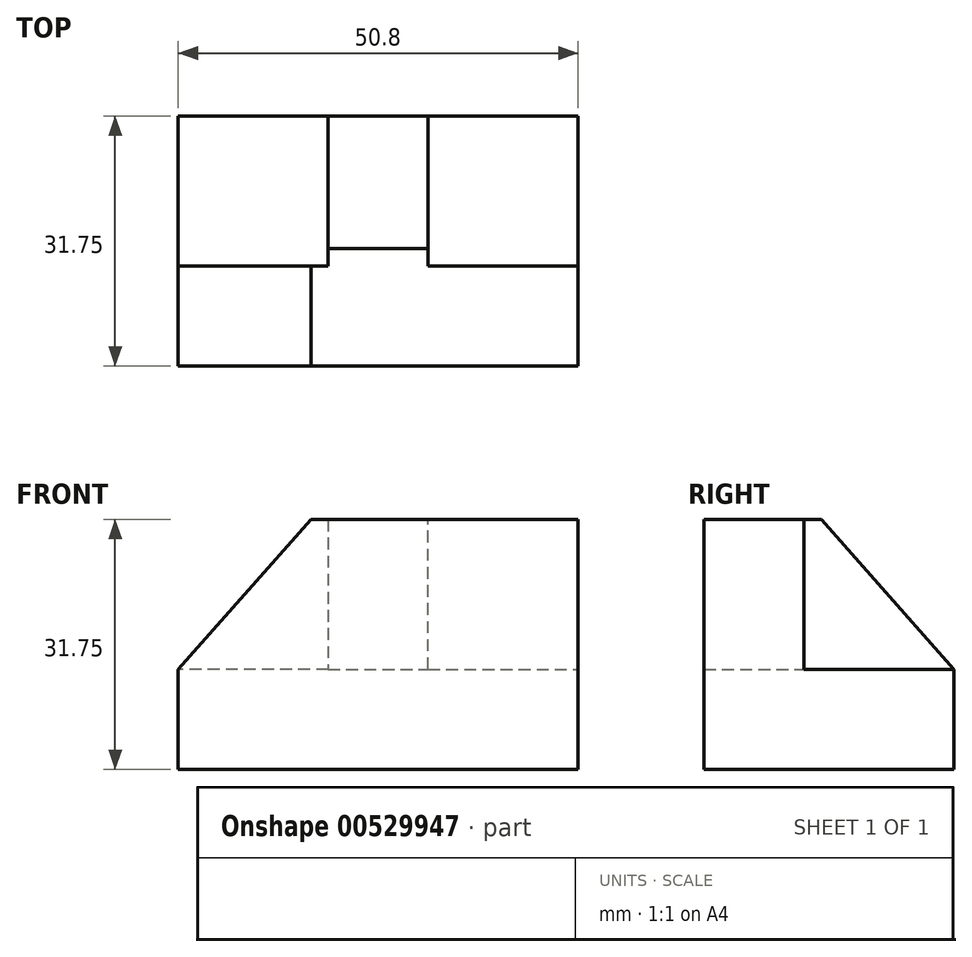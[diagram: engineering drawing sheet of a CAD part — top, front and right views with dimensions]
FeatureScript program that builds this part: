
annotation { "Feature Type Name" : "Feature", "Feature Type Description" : "" }
export const myFeature = defineFeature(function(context is Context, id is Id, definition is map)
    precondition{}
    {
        {
            var Q0;
            Q0=qCreatedBy(makeId("Front.planeOp"),FACE);
            var sketch = newSketch(context, id + "F0", { "sketchPlane" : qUnion([Q0])});
            skLineSegment(sketch, "E0", {"start": v(-58.65, 28.73) * mm, "end": v(-7.85, 28.73) * mm});
            skLineSegment(sketch, "E1", {"start": v(-7.85, 28.73) * mm, "end": v(-7.85, 60.48) * mm});
            skLineSegment(sketch, "E2", {"start": v(-7.85, 60.48) * mm, "end": v(-58.65, 60.48) * mm});
            skLineSegment(sketch, "E3", {"start": v(-58.65, 60.48) * mm, "end": v(-58.65, 28.73) * mm});
            skSolve(sketch);
        }
        {
            var Q0;
            Q0 = qSketchRegion(id + "F0", true);
            extrude(context, id + "F1", {"entities" : qUnion([Q0]), "depth" : 31.75 * mm, "offsetDistance" : 25.4 * mm});
        }
        {
            var Q0;
            Q0=makeQuery(id+"F1.opExtrude","SWEPT_FACE",FACE,{"disambiguationData":[OSD([sQuery(id+"F0.wireOp",EDGE,"E3")])]});
            var sketch = newSketch(context, id + "F2", { "sketchPlane" : qUnion([Q0])});
            skLineSegment(sketch, "E4", {"start": v(0, 28.73) * mm, "end": v(0, 41.46) * mm});
            skLineSegment(sketch, "E5", {"start": v(0, 41.46) * mm, "end": v(19.06, 41.46) * mm});
            skLineSegment(sketch, "E6", {"start": v(19.06, 41.46) * mm, "end": v(19.06, 60.48) * mm});
            skLineSegment(sketch, "E7", {"start": v(19.06, 60.48) * mm, "end": v(0, 60.48) * mm});
            skLineSegment(sketch, "E8", {"start": v(0, 60.48) * mm, "end": v(0, 41.46) * mm});
            skSolve(sketch);
        }
        {
            var Q0;
            Q0=makeQuery(id+"F2.imprint","IMPRINT",FACE,{"disambiguationData":[TD([[makeQuery(id+"F2.imprint","IMPRINT",EDGE,{"derivedFrom":sQuery(id+"F2.wireOp",EDGE,"E5")}),1.0]])]});
            extrude(context, id + "F3", {"entities" : qUnion([Q0]), "operationType" : NewBodyOperationType.REMOVE, "oppositeDirection" : true, "depth" : 19.05 * mm, "offsetDistance" : 25.4 * mm});
        }
        {
            var Q0;
            Q0=makeQuery(id+"F1.opExtrude","SWEPT_FACE",FACE,{"disambiguationData":[OSD([sQuery(id+"F0.wireOp",EDGE,"E1")])]});
            var sketch = newSketch(context, id + "F4", { "sketchPlane" : qUnion([Q0])});
            skLineSegment(sketch, "E9", {"start": v(0, 28.73) * mm, "end": v(0, 41.46) * mm});
            skLineSegment(sketch, "E10", {"start": v(0, 41.46) * mm, "end": v(-19.06, 41.46) * mm});
            skLineSegment(sketch, "E11", {"start": v(-19.06, 41.46) * mm, "end": v(-19.06, 60.48) * mm});
            skLineSegment(sketch, "E12", {"start": v(-19.06, 60.48) * mm, "end": v(0, 60.48) * mm});
            skLineSegment(sketch, "E13", {"start": v(0, 60.48) * mm, "end": v(0, 41.46) * mm});
            skSolve(sketch);
        }
        {
            var Q0;
            Q0=makeQuery(id+"F4.imprint","IMPRINT",FACE,{"disambiguationData":[TD([[makeQuery(id+"F4.imprint","IMPRINT",EDGE,{"derivedFrom":sQuery(id+"F4.wireOp",EDGE,"E10")}),-1.0]])]});
            extrude(context, id + "F5", {"entities" : qUnion([Q0]), "operationType" : NewBodyOperationType.REMOVE, "oppositeDirection" : true, "depth" : 19.05 * mm, "offsetDistance" : 25.4 * mm});
        }
        {
            var Q0;
            Q0=makeQuery(id+"F3.boolean.opBoolean","COPY",FACE,{"derivedFrom":makeQuery(id+"F3.opExtrude","SWEPT_FACE",FACE,{"disambiguationData":[OSD([sQuery(id+"F2.wireOp",EDGE,"E6")])]})});
            var sketch = newSketch(context, id + "F6", { "sketchPlane" : qUnion([Q0])});
            skLineSegment(sketch, "E14", {"start": v(58.65, 41.46) * mm, "end": v(41.8, 60.48) * mm});
            skLineSegment(sketch, "E15", {"start": v(41.8, 60.48) * mm, "end": v(58.65, 60.48) * mm});
            skLineSegment(sketch, "E16", {"start": v(58.65, 60.48) * mm, "end": v(58.65, 41.46) * mm});
            skSolve(sketch);
        }
        {
            var Q0;
            Q0=makeQuery(id+"F6.imprint","IMPRINT",FACE,{"disambiguationData":[TD([[makeQuery(id+"F6.imprint","IMPRINT",EDGE,{"derivedFrom":sQuery(id+"F6.wireOp",EDGE,"E14")}),-1.0]])]});
            extrude(context, id + "F7", {"entities" : qUnion([Q0]), "operationType" : NewBodyOperationType.REMOVE, "oppositeDirection" : true, "depth" : 25.4 * mm, "offsetDistance" : 25.4 * mm});
        }
        {
            var Q0;
            Q0=makeQuery(id+"F5.boolean.opBoolean","COPY",FACE,{"derivedFrom":makeQuery(id+"F5.opExtrude","CAP_FACE",FACE,{"disambiguationData":[OSD([sQuery(id+"F4.wireOp",EDGE,"E10"),sQuery(id+"F4.wireOp",EDGE,"E11"),sQuery(id+"F4.wireOp",EDGE,"E12"),sQuery(id+"F4.wireOp",EDGE,"E13")])],"isStart":false})});
            var sketch = newSketch(context, id + "F8", { "sketchPlane" : qUnion([Q0])});
            skLineSegment(sketch, "E17", {"start": v(0, 41.46) * mm, "end": v(-16.84, 60.48) * mm});
            skLineSegment(sketch, "E18", {"start": v(-16.84, 60.48) * mm, "end": v(0, 60.48) * mm});
            skLineSegment(sketch, "E19", {"start": v(0, 60.48) * mm, "end": v(0, 41.46) * mm});
            skSolve(sketch);
        }
        {
            var Q0;
            Q0=makeQuery(id+"F8.imprint","IMPRINT",FACE,{"disambiguationData":[TD([[makeQuery(id+"F8.imprint","IMPRINT",EDGE,{"derivedFrom":sQuery(id+"F8.wireOp",EDGE,"E17")}),-1.0]])]});
            extrude(context, id + "F9", {"entities" : qUnion([Q0]), "operationType" : NewBodyOperationType.REMOVE, "oppositeDirection" : true, "depth" : 25.4 * mm, "offsetDistance" : 25.4 * mm});
        }
    });
